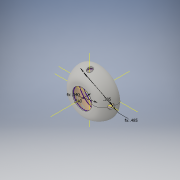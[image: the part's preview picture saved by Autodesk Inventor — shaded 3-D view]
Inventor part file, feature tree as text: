
AUTODESK INVENTOR PART (.ipt)
format: ipt  version: 2016 (Build 200138000, 138)  size: 439,296 bytes
history: native  units: in
note: dims shown in document units (in); Inventor stores cm internally (conversion verified against a paired STEP export)
features: other x5, plane x3, sketch x2, hole x2, thicken_offset x1, loft x1
ambient origin geometry x8: Origin, YZ Plane, XZ Plane, XY Plane, X Axis, Y Axis, Z Axis, Center Point
bodies: Body1 (feature_tree), Body2 (feature_tree)
feature tree (14):
  sketch  "Sketch1"  dims[d0=0.385in d1=0.485in]
  plane  "Work Plane1"
  plane  "Work Plane2"
  other  "Work Axis1"
  other  "Work Axis2"
  plane  "Work Plane5"
  thicken_offset  "Thicken3"
  other  "Work Point5"
  hole  "Hole4"  [1 undecoded]
  hole  "Hole5"  [1 undecoded]
  sketch  "Sketch2"  dims[d2=0.18in d3=0.24in d4=0.34in d5=0.0in d6=90.0deg d7=0.0in d8=90.0deg d9=0.0in d10=90.0deg d11=0.0in d12=90.0deg d13=0.1in d21=0.015in d22=0.015in d70=1.0in d71=1.0in d54=0.06in d55=0.75in d56=0.375in d57=0.25in d58=0.5635in d59=0.1in d60=0.0in d72=1.0in d73=1.0in d63=0.06in d64=0.75in d65=0.375in d66=0.25in d67=0.5635in d68=0.1in d69=0.0in]
  other  "Srf1"
  other  "Work Point3"
  loft  "LoftSrf1"
note: 2 required parameter values undecoded (feature->parameter linkage not recoverable at this tier; creation-order binding heuristic only, values carry confidence <= 0.55)
